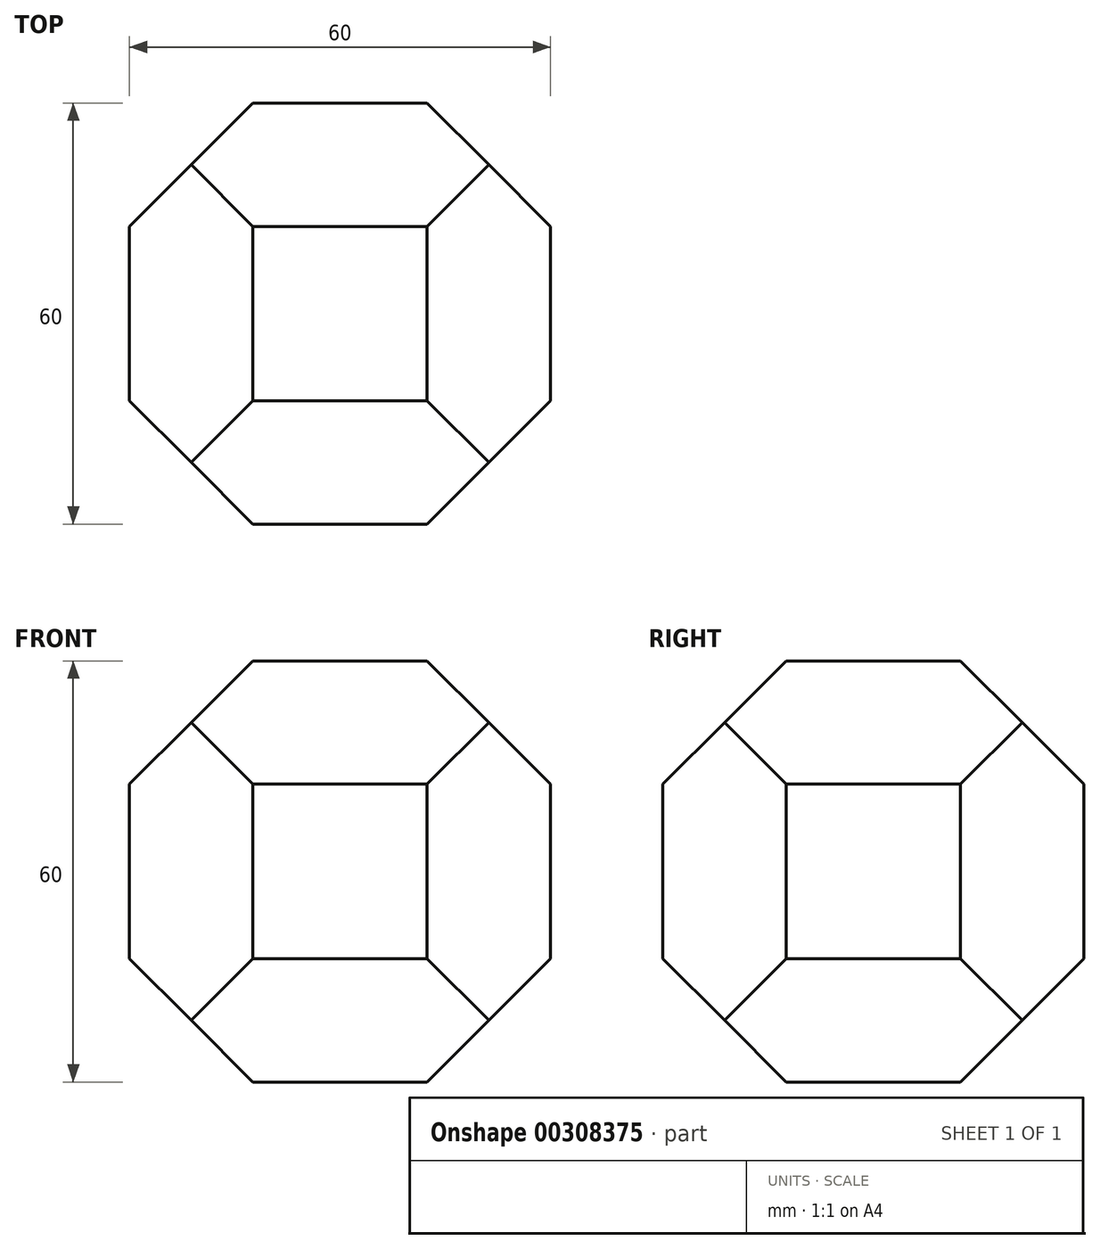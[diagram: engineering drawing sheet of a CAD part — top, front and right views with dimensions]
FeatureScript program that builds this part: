
annotation { "Feature Type Name" : "Feature", "Feature Type Description" : "" }
export const myFeature = defineFeature(function(context is Context, id is Id, definition is map)
    precondition{}
    {
        {
            var Q0;
            Q0=qCreatedBy(makeId("Front.planeOp"),FACE);
            var sketch = newSketch(context, id + "F0", { "sketchPlane" : qUnion([Q0])});
            skCircle(sketch, "E0.cCircle", {"center": v(0, 0) * mm, "radius": 30 * mm, "construction": true});
            skLineSegment(sketch, "E0.0", {"start": v(-30, -12.43) * mm, "end": v(-30, 12.43) * mm});
            skLineSegment(sketch, "E0.1", {"start": v(-30, 12.43) * mm, "end": v(-12.43, 30) * mm});
            skLineSegment(sketch, "E0.2", {"start": v(-12.43, 30) * mm, "end": v(12.43, 30) * mm});
            skLineSegment(sketch, "E0.3", {"start": v(12.43, 30) * mm, "end": v(30, 12.43) * mm});
            skLineSegment(sketch, "E0.4", {"start": v(30, 12.43) * mm, "end": v(30, -12.43) * mm});
            skLineSegment(sketch, "E0.5", {"start": v(30, -12.43) * mm, "end": v(12.43, -30) * mm});
            skLineSegment(sketch, "E0.6", {"start": v(12.43, -30) * mm, "end": v(-12.43, -30) * mm});
            skLineSegment(sketch, "E0.7", {"start": v(-12.43, -30) * mm, "end": v(-30, -12.43) * mm});
            skPoint(sketch, "E0.0.midPoint", {"position": v(-30, 0) * mm});
            skSolve(sketch);
        }
        {
            var Q0;
            Q0=qCreatedBy(makeId("Top.planeOp"),FACE);
            var sketch = newSketch(context, id + "F1", { "sketchPlane" : qUnion([Q0])});
            skCircle(sketch, "E1.cCircle", {"center": v(0, 0) * mm, "radius": 30 * mm, "construction": true});
            skLineSegment(sketch, "E1.0", {"start": v(30, 12.43) * mm, "end": v(30, -12.43) * mm});
            skLineSegment(sketch, "E1.1", {"start": v(30, -12.43) * mm, "end": v(12.43, -30) * mm});
            skLineSegment(sketch, "E1.2", {"start": v(12.43, -30) * mm, "end": v(-12.43, -30) * mm});
            skLineSegment(sketch, "E1.3", {"start": v(-12.43, -30) * mm, "end": v(-30, -12.43) * mm});
            skLineSegment(sketch, "E1.4", {"start": v(-30, -12.43) * mm, "end": v(-30, 12.43) * mm});
            skLineSegment(sketch, "E1.5", {"start": v(-30, 12.43) * mm, "end": v(-12.43, 30) * mm});
            skLineSegment(sketch, "E1.6", {"start": v(-12.43, 30) * mm, "end": v(12.43, 30) * mm});
            skLineSegment(sketch, "E1.7", {"start": v(12.43, 30) * mm, "end": v(30, 12.43) * mm});
            skPoint(sketch, "E1.0.midPoint", {"position": v(30, 0) * mm});
            skSolve(sketch);
        }
        {
            var Q0;
            Q0=qCreatedBy(makeId("Right.planeOp"),FACE);
            var sketch = newSketch(context, id + "F2", { "sketchPlane" : qUnion([Q0])});
            skCircle(sketch, "E2.cCircle", {"center": v(0, 0) * mm, "radius": 30 * mm, "construction": true});
            skLineSegment(sketch, "E2.0", {"start": v(-12.43, 30) * mm, "end": v(12.43, 30) * mm});
            skLineSegment(sketch, "E2.1", {"start": v(12.43, 30) * mm, "end": v(30, 12.43) * mm});
            skLineSegment(sketch, "E2.2", {"start": v(30, 12.43) * mm, "end": v(30, -12.43) * mm});
            skLineSegment(sketch, "E2.3", {"start": v(30, -12.43) * mm, "end": v(12.43, -30) * mm});
            skLineSegment(sketch, "E2.4", {"start": v(12.43, -30) * mm, "end": v(-12.43, -30) * mm});
            skLineSegment(sketch, "E2.5", {"start": v(-12.43, -30) * mm, "end": v(-30, -12.43) * mm});
            skLineSegment(sketch, "E2.6", {"start": v(-30, -12.43) * mm, "end": v(-30, 12.43) * mm});
            skLineSegment(sketch, "E2.7", {"start": v(-30, 12.43) * mm, "end": v(-12.43, 30) * mm});
            skPoint(sketch, "E2.0.midPoint", {"position": v(0, 30) * mm});
            skSolve(sketch);
        }
        {
            var Q0;
            Q0 = qSketchRegion(id + "F0", true);
            extrude(context, id + "F3", {"entities" : qUnion([Q0]), "endBound" : BoundingType.SYMMETRIC, "depth" : 60 * mm});
        }
        {
            var Q0;
            Q0 = qSketchRegion(id + "F1", true);
            extrude(context, id + "F4", {"entities" : qUnion([Q0]), "operationType" : NewBodyOperationType.INTERSECT, "endBound" : BoundingType.SYMMETRIC, "depth" : 60 * mm});
        }
        {
            var Q0;
            Q0 = qSketchRegion(id + "F2", true);
            extrude(context, id + "F5", {"entities" : qUnion([Q0]), "operationType" : NewBodyOperationType.INTERSECT, "endBound" : BoundingType.SYMMETRIC, "depth" : 60 * mm});
        }
    });
